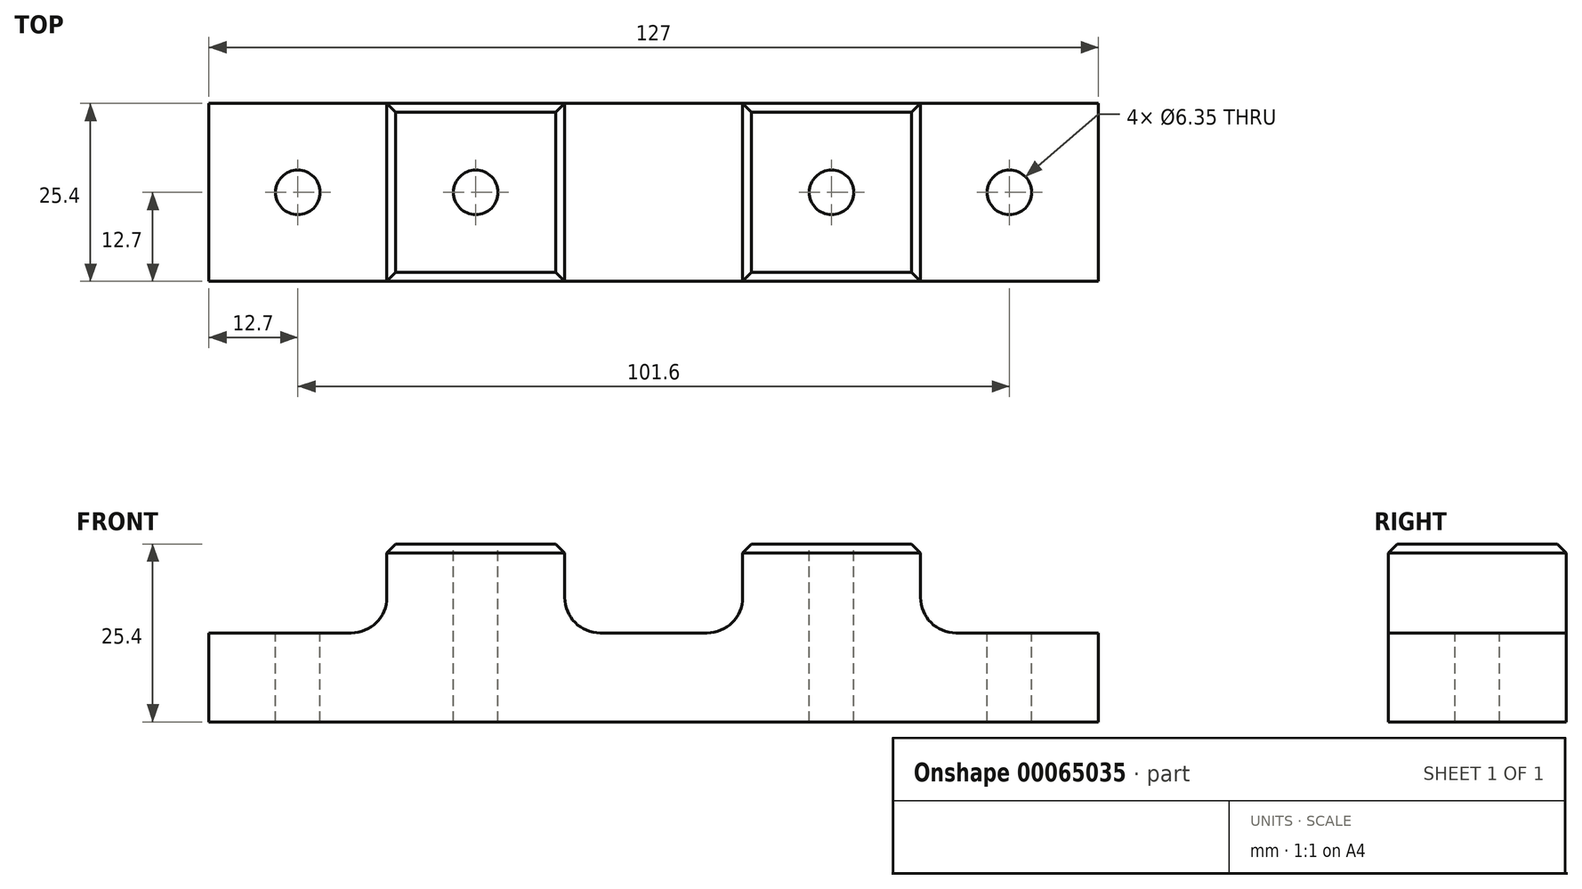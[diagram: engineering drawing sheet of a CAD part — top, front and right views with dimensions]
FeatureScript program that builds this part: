
annotation { "Feature Type Name" : "Feature", "Feature Type Description" : "" }
export const myFeature = defineFeature(function(context is Context, id is Id, definition is map)
    precondition{}
    {
        {
            var Q0;
            Q0=qCreatedBy(makeId("Front.planeOp"),FACE);
            var sketch = newSketch(context, id + "F0", { "sketchPlane" : qUnion([Q0])});
            skLineSegment(sketch, "E0", {"start": v(-63.5, 0) * mm, "end": v(63.5, 0) * mm});
            skLineSegment(sketch, "E1", {"start": v(63.5, 0) * mm, "end": v(63.5, 12.7) * mm});
            skLineSegment(sketch, "E2", {"start": v(63.5, 12.7) * mm, "end": v(38.1, 12.7) * mm});
            skLineSegment(sketch, "E3", {"start": v(38.1, 12.7) * mm, "end": v(38.1, 25.4) * mm});
            skLineSegment(sketch, "E4", {"start": v(38.1, 25.4) * mm, "end": v(12.7, 25.4) * mm});
            skLineSegment(sketch, "E5", {"start": v(12.7, 25.4) * mm, "end": v(12.7, 12.7) * mm});
            skLineSegment(sketch, "E6", {"start": v(12.7, 12.7) * mm, "end": v(-12.7, 12.7) * mm});
            skLineSegment(sketch, "E7", {"start": v(-12.7, 12.7) * mm, "end": v(-12.7, 25.4) * mm});
            skLineSegment(sketch, "E8", {"start": v(-12.7, 25.4) * mm, "end": v(-38.1, 25.4) * mm});
            skLineSegment(sketch, "E9", {"start": v(-38.1, 25.4) * mm, "end": v(-38.1, 12.7) * mm});
            skLineSegment(sketch, "E10", {"start": v(-38.1, 12.7) * mm, "end": v(-63.5, 12.7) * mm});
            skLineSegment(sketch, "E11", {"start": v(-63.5, 12.7) * mm, "end": v(-63.5, 0) * mm});
            skSolve(sketch);
        }
        {
            var Q0;
            Q0=makeQuery(id+"F0.imprint","IMPRINT",FACE,{"disambiguationData":[TD([[makeQuery(id+"F0.imprint","IMPRINT",EDGE,{"derivedFrom":sQuery(id+"F0.wireOp",EDGE,"E0")}),1.0]])]});
            extrude(context, id + "F1", {"entities" : qUnion([Q0]), "depth" : 12.7 * mm, "hasSecondDirection" : true, "secondDirectionOppositeDirection" : true, "secondDirectionDepth" : 12.7 * mm});
        }
        {
            var Q0;
            Q0=makeQuery(id+"F1.opExtrude","SWEPT_FACE",FACE,{"disambiguationData":[OSD([sQuery(id+"F0.wireOp",EDGE,"E6")])]});
            var sketch = newSketch(context, id + "F2", { "sketchPlane" : qUnion([Q0])});
            skCircle(sketch, "E12", {"center": v(-50.8, 0) * mm, "radius": 3.18 * mm});
            skCircle(sketch, "E13", {"center": v(50.8, 0) * mm, "radius": 3.18 * mm});
            skCircle(sketch, "E14", {"center": v(-25.4, 0) * mm, "radius": 3.18 * mm});
            skCircle(sketch, "E15", {"center": v(25.4, 0) * mm, "radius": 3.18 * mm});
            skSolve(sketch);
        }
        {
            var Q0;
            Q0 = qSketchRegion(id + "F2", true);
            extrude(context, id + "F3", {"entities" : qUnion([Q0]), "operationType" : NewBodyOperationType.REMOVE, "endBound" : BoundingType.THROUGH_ALL, "oppositeDirection" : true, "depth" : 25.4 * mm, "hasSecondDirection" : true, "secondDirectionBound" : SecondDirectionBoundingType.THROUGH_ALL, "secondDirectionOppositeDirection" : false, "secondDirectionDepth" : 25.4 * mm});
        }
        {
            var Q0;
            Q0=makeQuery(id+"F1.opExtrude","SWEPT_EDGE",EDGE,{"disambiguationData":[OSD([sQuery(id+"F0.wireOp",EDGE,"E9"),sQuery(id+"F0.wireOp",EDGE,"E10")])]});
            var Q1;
            Q1=makeQuery(id+"F1.opExtrude","SWEPT_EDGE",EDGE,{"disambiguationData":[OSD([sQuery(id+"F0.wireOp",EDGE,"E5"),sQuery(id+"F0.wireOp",EDGE,"E6")])]});
            var Q2;
            Q2=makeQuery(id+"F1.opExtrude","SWEPT_EDGE",EDGE,{"disambiguationData":[OSD([sQuery(id+"F0.wireOp",EDGE,"E6"),sQuery(id+"F0.wireOp",EDGE,"E7")])]});
            var Q3;
            Q3=makeQuery(id+"F1.opExtrude","SWEPT_EDGE",EDGE,{"disambiguationData":[OSD([sQuery(id+"F0.wireOp",EDGE,"E2"),sQuery(id+"F0.wireOp",EDGE,"E3")])]});
            fillet(context, id + "F4", {"entities" : qUnion([Q0, Q1, Q2, Q3]), "radius" : 5.08 * mm, "tangentPropagation" : true, "allowEdgeOverflow" : false});
        }
        {
            var Q0;
            Q0=makeQuery(id+"F1.opExtrude","CAP_EDGE",EDGE,{"disambiguationData":[OSD([sQuery(id+"F0.wireOp",EDGE,"E8")])],"isStart":false});
            var Q1;
            Q1=makeQuery(id+"F1.opExtrude","SWEPT_EDGE",EDGE,{"disambiguationData":[OSD([sQuery(id+"F0.wireOp",EDGE,"E7"),sQuery(id+"F0.wireOp",EDGE,"E8")])]});
            var Q2;
            Q2=makeQuery(id+"F1.opExtrude","CAP_EDGE",EDGE,{"disambiguationData":[OSD([sQuery(id+"F0.wireOp",EDGE,"E8")])],"isStart":true});
            var Q3;
            Q3=makeQuery(id+"F1.opExtrude","SWEPT_EDGE",EDGE,{"disambiguationData":[OSD([sQuery(id+"F0.wireOp",EDGE,"E8"),sQuery(id+"F0.wireOp",EDGE,"E9")])]});
            var Q4;
            Q4=makeQuery(id+"F1.opExtrude","SWEPT_EDGE",EDGE,{"disambiguationData":[OSD([sQuery(id+"F0.wireOp",EDGE,"E4"),sQuery(id+"F0.wireOp",EDGE,"E5")])]});
            var Q5;
            Q5=makeQuery(id+"F1.opExtrude","CAP_EDGE",EDGE,{"disambiguationData":[OSD([sQuery(id+"F0.wireOp",EDGE,"E4")])],"isStart":true});
            var Q6;
            Q6=makeQuery(id+"F1.opExtrude","SWEPT_EDGE",EDGE,{"disambiguationData":[OSD([sQuery(id+"F0.wireOp",EDGE,"E3"),sQuery(id+"F0.wireOp",EDGE,"E4")])]});
            var Q7;
            Q7=makeQuery(id+"F1.opExtrude","CAP_EDGE",EDGE,{"disambiguationData":[OSD([sQuery(id+"F0.wireOp",EDGE,"E4")])],"isStart":false});
            chamfer(context, id + "F5", {"entities" : qUnion([Q0, Q1, Q2, Q3, Q4, Q5, Q6, Q7]), "width" : 1.27 * mm, "tangentPropagation" : true});
        }
    });
